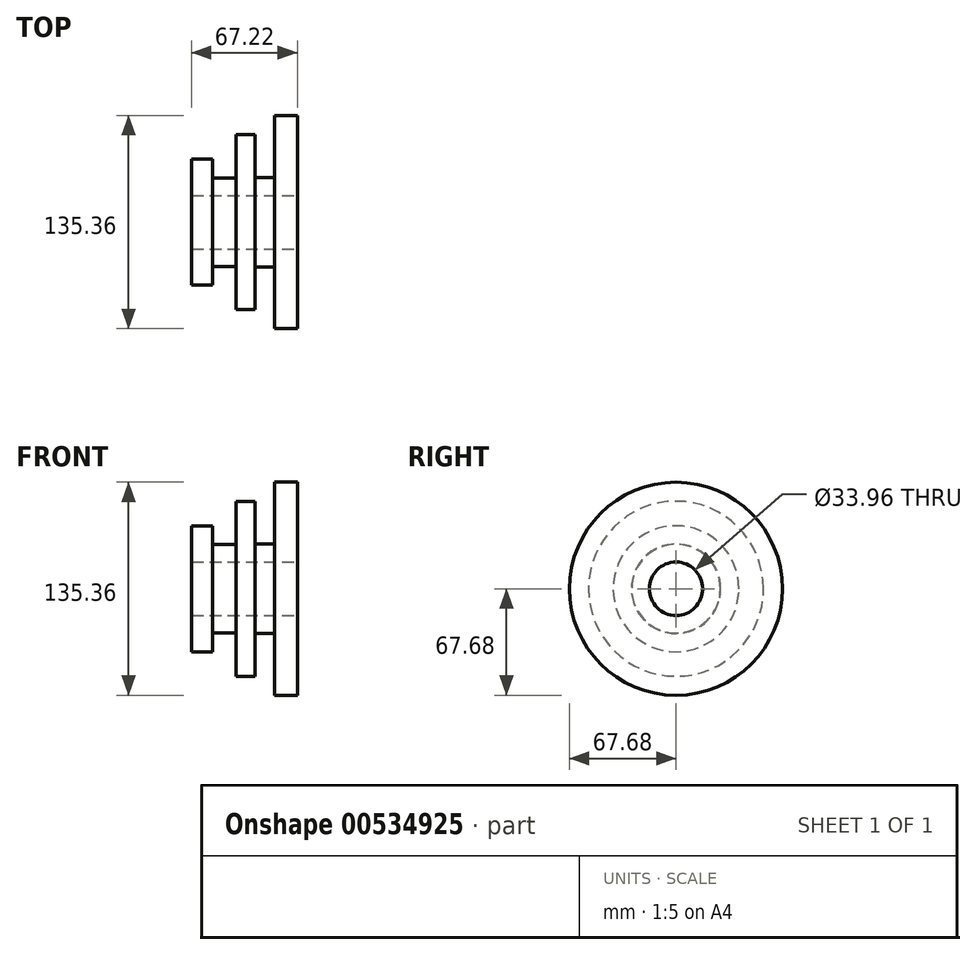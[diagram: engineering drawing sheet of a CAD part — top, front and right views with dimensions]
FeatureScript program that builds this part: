
annotation { "Feature Type Name" : "Feature", "Feature Type Description" : "" }
export const myFeature = defineFeature(function(context is Context, id is Id, definition is map)
    precondition{}
    {
        {
            var Q0;
            Q0=qCreatedBy(makeId("Front.planeOp"),FACE);
            var sketch = newSketch(context, id + "F0", { "sketchPlane" : qUnion([Q0])});
            skLineSegment(sketch, "E0", {"start": v(0, 0) * mm, "end": v(-114.43, 0) * mm});
            skLineSegment(sketch, "E1", {"start": v(0, 16.98) * mm, "end": v(-67.22, 16.98) * mm});
            skLineSegment(sketch, "E2", {"start": v(-67.22, 16.98) * mm, "end": v(-67.22, 40) * mm});
            skLineSegment(sketch, "E3", {"start": v(-67.22, 40) * mm, "end": v(-53.96, 40) * mm});
            skLineSegment(sketch, "E4", {"start": v(-53.96, 40) * mm, "end": v(-53.96, 28.14) * mm});
            skLineSegment(sketch, "E5", {"start": v(-53.96, 28.14) * mm, "end": v(-39.07, 28.14) * mm});
            skLineSegment(sketch, "E6", {"start": v(-39.07, 28.14) * mm, "end": v(-39.07, 55.59) * mm});
            skLineSegment(sketch, "E7", {"start": v(-39.07, 55.59) * mm, "end": v(-26.75, 55.59) * mm});
            skLineSegment(sketch, "E8", {"start": v(-26.75, 55.59) * mm, "end": v(-26.75, 28.38) * mm});
            skLineSegment(sketch, "E9", {"start": v(-26.75, 28.38) * mm, "end": v(-14.42, 28.38) * mm});
            skLineSegment(sketch, "E10", {"start": v(-14.42, 28.38) * mm, "end": v(-14.42, 67.68) * mm});
            skLineSegment(sketch, "E11", {"start": v(-14.42, 67.68) * mm, "end": v(0, 67.68) * mm});
            skLineSegment(sketch, "E12", {"start": v(0, 67.68) * mm, "end": v(0, 16.98) * mm});
            skSolve(sketch);
        }
        {
            var Q0;
            Q0=makeQuery(id+"F0.imprint","IMPRINT",FACE,{"disambiguationData":[TD([[makeQuery(id+"F0.imprint","IMPRINT",EDGE,{"derivedFrom":sQuery(id+"F0.wireOp",EDGE,"E1")}),-1.0]])]});
            var Q1;
            Q1=sQuery(id+"F0.wireOp",EDGE,"E0");
            revolve(context, id + "F1", {"entities" : qUnion([Q0]), "axis" : qUnion([Q1]), "revolveType" : RevolveType.FULL});
        }
    });
